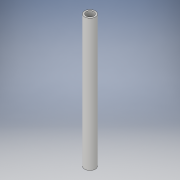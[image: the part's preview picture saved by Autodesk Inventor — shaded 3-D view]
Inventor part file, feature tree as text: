
AUTODESK INVENTOR PART (.ipt)
format: ipt  version: 2019.4 (Build 234330000, 330)  size: 93,184 bytes
history: native  units: mm
features: extrude x1, sketch x1
ambient origin geometry x8: Origin, YZ Plane, XZ Plane, XY Plane, X Axis, Y Axis, Z Axis, Center Point
bodies: Solid1 (feature_tree)
feature tree (2):
  extrude  "Extrusion1"  Depth=85.75mm
  sketch  "Sketch1"  dims[d0=5.0mm d1=7.0mm d2=85.75mm d3=0.0mm]
